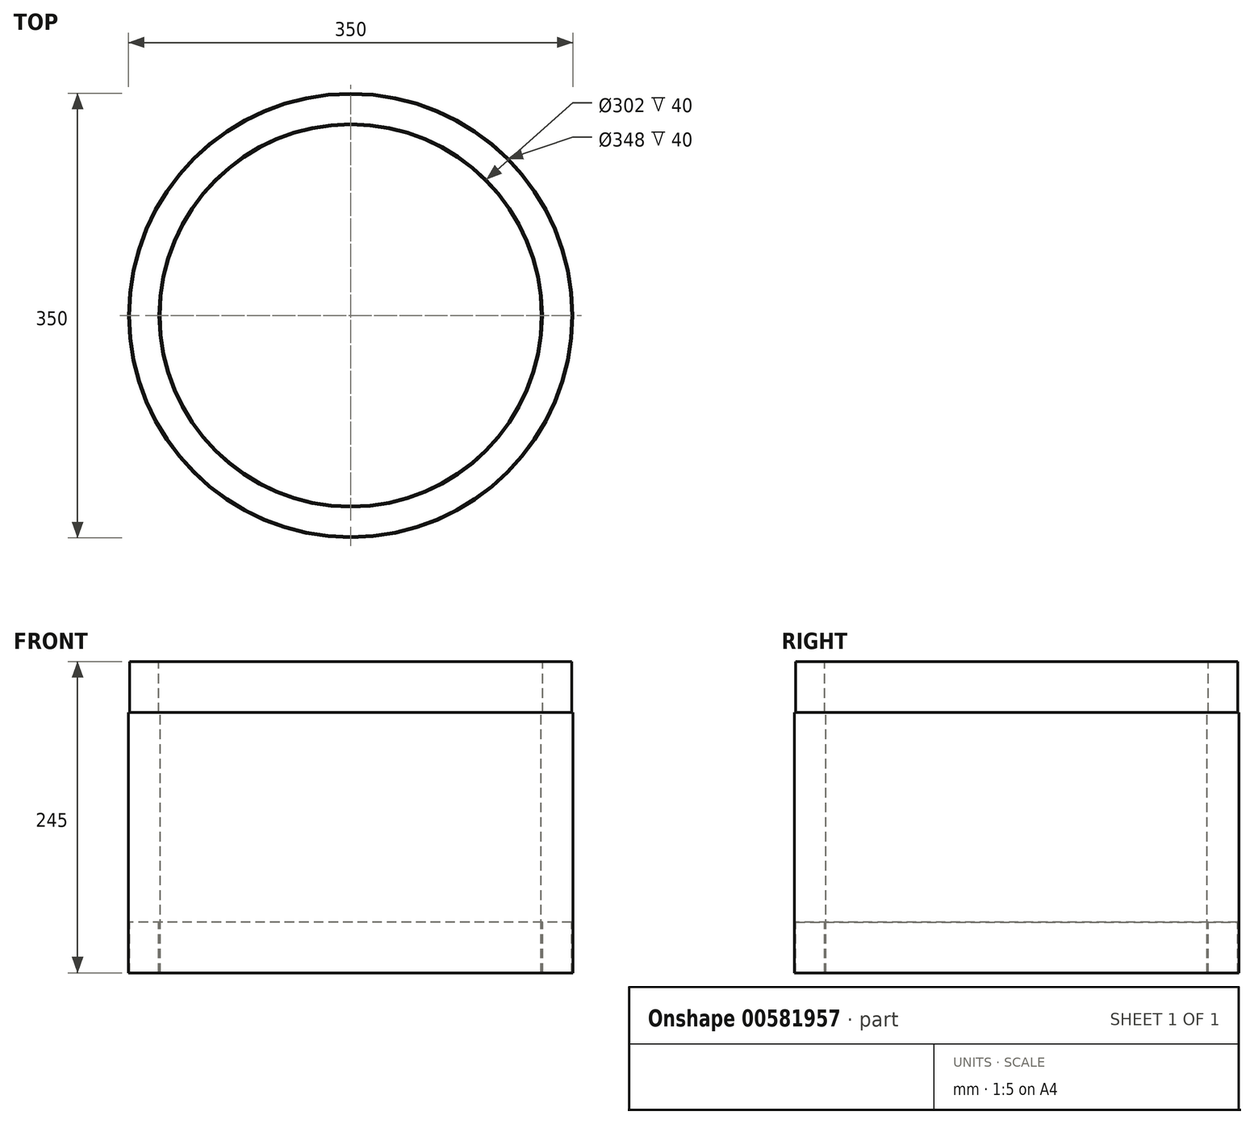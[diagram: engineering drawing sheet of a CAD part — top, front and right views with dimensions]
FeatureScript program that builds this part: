
annotation { "Feature Type Name" : "Feature", "Feature Type Description" : "" }
export const myFeature = defineFeature(function(context is Context, id is Id, definition is map)
    precondition{}
    {
        {
            var Q0;
            Q0=qCreatedBy(makeId("Front.planeOp"),FACE);
            var sketch = newSketch(context, id + "F0", { "sketchPlane" : qUnion([Q0])});
            skLineSegment(sketch, "E0", {"start": v(0, 345.75) * mm, "end": v(0, -558.03) * mm, "construction": true});
            skLineSegment(sketch, "E1", {"start": v(-150, -518.84) * mm, "end": v(-150, -313.84) * mm});
            skLineSegment(sketch, "E2", {"start": v(-150, -313.84) * mm, "end": v(-151, -313.84) * mm});
            skLineSegment(sketch, "E3", {"start": v(-151, -313.84) * mm, "end": v(-151, -273.84) * mm});
            skLineSegment(sketch, "E4", {"start": v(-151, -273.84) * mm, "end": v(-174, -273.84) * mm});
            skLineSegment(sketch, "E5", {"start": v(-174, -273.84) * mm, "end": v(-174, -313.84) * mm});
            skLineSegment(sketch, "E6", {"start": v(-174, -313.84) * mm, "end": v(-175, -313.84) * mm});
            skLineSegment(sketch, "E7", {"start": v(-175, -313.84) * mm, "end": v(-175, -518.84) * mm});
            skLineSegment(sketch, "E8", {"start": v(-175, -518.84) * mm, "end": v(-174, -518.84) * mm});
            skLineSegment(sketch, "E9", {"start": v(-174, -518.84) * mm, "end": v(-174, -478.84) * mm});
            skLineSegment(sketch, "E10", {"start": v(-174, -478.84) * mm, "end": v(-151, -478.84) * mm});
            skLineSegment(sketch, "E11", {"start": v(-151, -478.84) * mm, "end": v(-151, -518.84) * mm});
            skLineSegment(sketch, "E12", {"start": v(-151, -518.84) * mm, "end": v(-150, -518.84) * mm});
            skSolve(sketch);
        }
        {
            var Q0;
            Q0=qSketchRegion(id+"F0",true);
            var Q1;
            Q1=sQuery(id+"F0.wireOp",EDGE,"E0");
            revolve(context, id + "F1", {"entities" : qUnion([Q0]), "axis" : qUnion([Q1]), "revolveType" : RevolveType.FULL});
        }
    });
